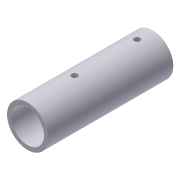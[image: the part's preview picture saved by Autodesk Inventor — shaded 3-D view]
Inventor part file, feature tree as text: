
AUTODESK INVENTOR PART (.ipt)
format: ipt  version: 2012 (Build 160160000, 160)  size: 91,136 bytes
history: native  units: in
note: dims shown in document units (in); Inventor stores cm internally (conversion verified against a paired STEP export)
features: extrude x2, sketch x2, plane x1, pattern_linear x1, other x1, projected_geometry x1
ambient origin geometry x8: Origin, YZ Plane, XZ Plane, XY Plane, X Axis, Y Axis, Z Axis, Center Point
bodies: Solid1 (feature_tree)
feature tree (8):
  extrude  "Extrusion1"  Depth=1.315in
  plane  "Work Plane1"
  extrude  "Extrusion2"  TaperAngle=90.0deg  [1 undecoded]
  pattern_linear  "Rectangular Pattern1"  Spacing1=1.5in  [1 undecoded]
  sketch  "Sketch1"  dims[d0=1.049in d1=1.315in]
  other  "Work Axis1"
  sketch  "Sketch2"  dims[d2=4.0in d3=0.0in d4=90.0deg d5=1.5in d6=0.191in d7=64.5in d8=0.0in d9=0.7874in d11=2.0in]
  projected_geometry  "Projected Loop1"
note: 2 required parameter values undecoded (feature->parameter linkage not recoverable at this tier; creation-order binding heuristic only, values carry confidence <= 0.55)
